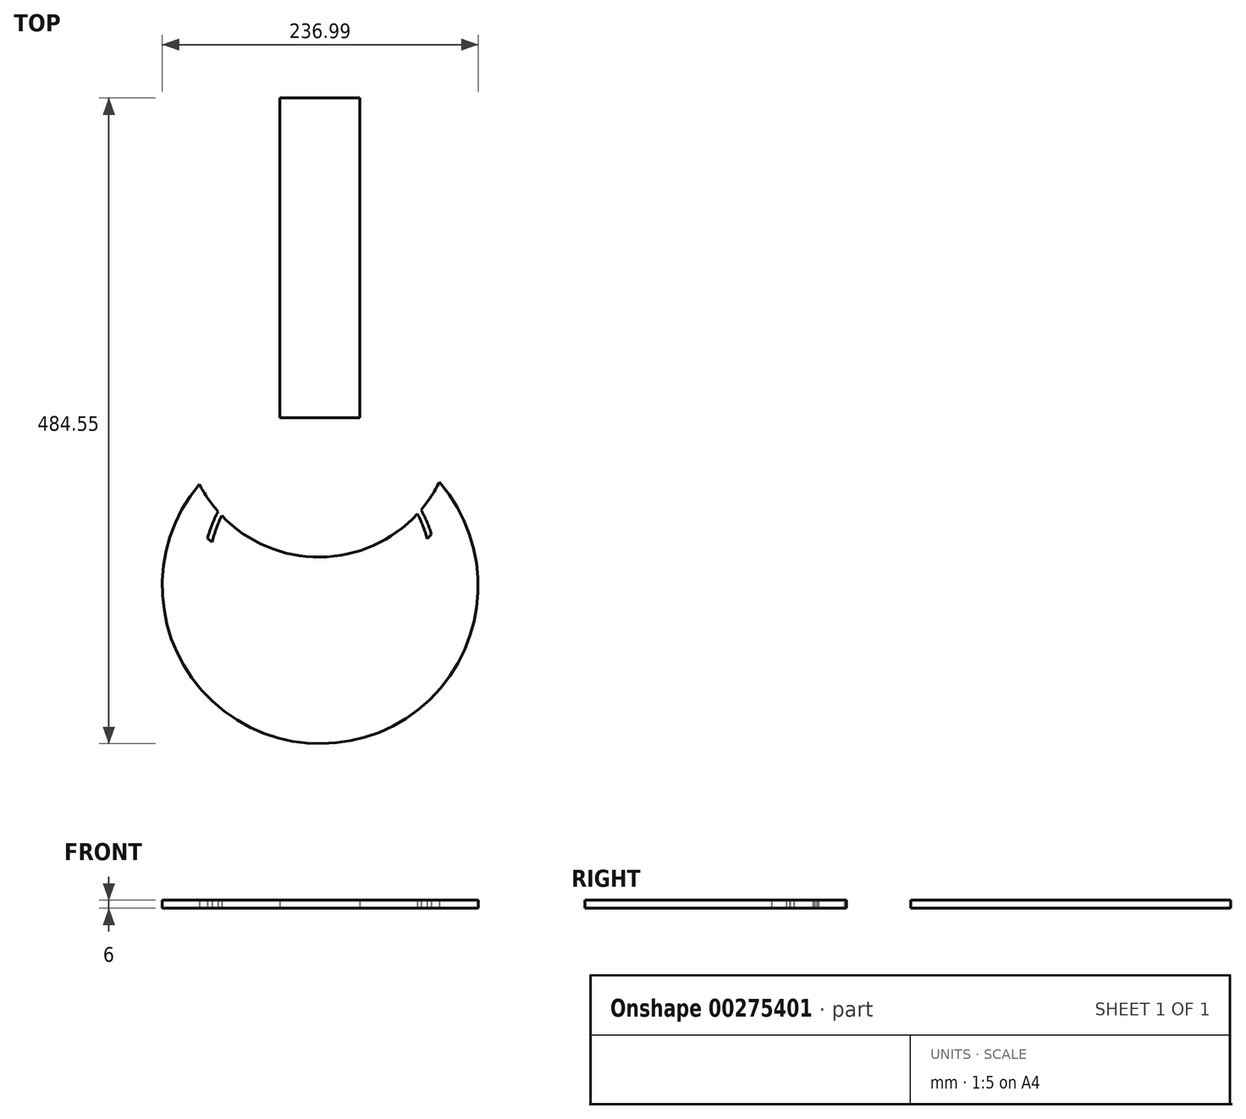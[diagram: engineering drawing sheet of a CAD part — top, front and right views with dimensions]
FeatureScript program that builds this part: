
annotation { "Feature Type Name" : "Feature", "Feature Type Description" : "" }
export const myFeature = defineFeature(function(context is Context, id is Id, definition is map)
    precondition{}
    {
        {
            var Q0;
            Q0=qCreatedBy(makeId("Top.planeOp"),FACE);
            var sketch = newSketch(context, id + "F0", { "sketchPlane" : qUnion([Q0])});
            skLineSegment(sketch, "E0.bottom", {"start": v(-25.11, 155.22) * mm, "end": v(34.89, 155.22) * mm});
            skLineSegment(sketch, "E1", {"start": v(-25.11, -64.78) * mm, "end": v(34.89, -64.78) * mm});
            skPoint(sketch, "E2.start.orphan", {"position": v(-125, -132.75) * mm});
            skLineSegment(sketch, "E3", {"start": v(0, 0) * mm, "end": v(4.89, -189.33) * mm, "construction": true});
            skPoint(sketch, "E3.endSnap0", {"position": v(4.89, -64.78) * mm});
            skLineSegment(sketch, "E4", {"start": v(4.89, -189.33) * mm, "end": v(5.87, -312.36) * mm});
            skPoint(sketch, "E4.endSnap0", {"position": v(5.87, -212.77) * mm});
            skArc(sketch, "E5", {"start": v(-85.55, -134.55) * mm, "mid": v(6.15, -329.32) * mm, "end": v(94.46, -133) * mm});
            skArc(sketch, "E6", {"start": v(-85.55, -134.55) * mm, "mid": v(4.94, -189.33) * mm, "end": v(94.46, -133) * mm});
            skPoint(sketch, "E7.startSnap0", {"position": v(4.94, -189.33) * mm});
            skLineSegment(sketch, "E8.bottom", {"start": v(-25.11, -64.78) * mm, "end": v(-25.11, -64.78) * mm});
            skLineSegment(sketch, "E9.bottom", {"start": v(34.89, -64.78) * mm, "end": v(34.89, -64.78) * mm});
            skLineSegment(sketch, "E10", {"start": v(34.89, -64.78) * mm, "end": v(34.14, -184.74) * mm});
            skLineSegment(sketch, "E11", {"start": v(-25.11, -64.78) * mm, "end": v(-25.86, -184.78) * mm});
            skLineSegment(sketch, "E12", {"start": v(34.89, 155.22) * mm, "end": v(34.89, -64.78) * mm});
            skLineSegment(sketch, "E13", {"start": v(-25.11, -64.78) * mm, "end": v(-25.11, 155.22) * mm});
            skLineSegment(sketch, "E14", {"start": v(-25.11, -64.78) * mm, "end": v(-25.24, -84.78) * mm});
            skLineSegment(sketch, "E15", {"start": v(-25.24, -84.78) * mm, "end": v(34.76, -84.78) * mm});
            skLineSegment(sketch, "E16", {"start": v(34.76, -84.78) * mm, "end": v(34.89, -64.78) * mm});
            skArc(sketch, "E17", {"start": v(-71.48, -155.21) * mm, "mid": v(5.76, -284.64) * mm, "end": v(80.75, -153.9) * mm});
            skArc(sketch, "E18", {"start": v(-68.72, -158.21) * mm, "mid": v(5.77, -278.56) * mm, "end": v(78.1, -156.9) * mm});
            skLineSegment(sketch, "E19", {"start": v(-79.46, -175.21) * mm, "end": v(-75.86, -178.21) * mm});
            skLineSegment(sketch, "E20", {"start": v(85.29, -175.56) * mm, "end": v(88.65, -172.27) * mm});
            skSolve(sketch);
        }
        {
            var Q0;
            Q0=makeQuery(id+"F0.imprint","IMPRINT",FACE,{"disambiguationData":[TD([[makeQuery(id+"F0.imprint","IMPRINT",EDGE,{"derivedFrom":sQuery(id+"F0.wireOp",EDGE,"E0.bottom")}),-1.0]])]});
            var Q1;
            {var subQ1=sQuery(id+"F0.wireOp",EDGE,"E5");Q1=makeQuery(id+"F0.imprint","IMPRINT",FACE,{"disambiguationData":[TD([[makeQuery(id+"F0.imprint","IMPRINT",EDGE,{"derivedFrom":subQ1}),1.0]])]});}
            var Q2;
            {var subQ0=sQuery(id+"F0.wireOp",EDGE,"E6");var subQ1=sQuery(id+"F0.wireOp",EDGE,"E4");var subQ2=makeQuery(id+"F0.imprint","INTERSECT",VERTEX,{"derivedFrom":[subQ1,subQ0]});Q2=makeQuery(id+"F0.imprint","IMPRINT",FACE,{"disambiguationData":[TD([[makeQuery(id+"F0.imprint","IMPRINT",EDGE,{"disambiguationData":[TD([[subQ2,-1.0]])],"derivedFrom":subQ1}),-1.0]])]});}
            var Q3;
            {var subQ0=sQuery(id+"F0.wireOp",EDGE,"E6");var subQ1=sQuery(id+"F0.wireOp",EDGE,"E4");var subQ2=makeQuery(id+"F0.imprint","INTERSECT",VERTEX,{"derivedFrom":[subQ1,subQ0]});Q3=makeQuery(id+"F0.imprint","IMPRINT",FACE,{"disambiguationData":[TD([[makeQuery(id+"F0.imprint","IMPRINT",EDGE,{"disambiguationData":[TD([[subQ2,-1.0]])],"derivedFrom":subQ1}),1.0]])]});}
            var Q4;
            {var subQ0=sQuery(id+"F0.wireOp",EDGE,"E17");var subQ1=sQuery(id+"F0.wireOp",EDGE,"E4");var subQ2=makeQuery(id+"F0.imprint","INTERSECT",VERTEX,{"derivedFrom":[subQ1,subQ0]});Q4=makeQuery(id+"F0.imprint","IMPRINT",FACE,{"disambiguationData":[TD([[makeQuery(id+"F0.imprint","IMPRINT",EDGE,{"disambiguationData":[TD([[subQ2,1.0]])],"derivedFrom":subQ1}),-1.0]])]});}
            var Q5;
            {var subQ0=sQuery(id+"F0.wireOp",EDGE,"E17");var subQ1=sQuery(id+"F0.wireOp",EDGE,"E4");var subQ2=makeQuery(id+"F0.imprint","INTERSECT",VERTEX,{"derivedFrom":[subQ1,subQ0]});Q5=makeQuery(id+"F0.imprint","IMPRINT",FACE,{"disambiguationData":[TD([[makeQuery(id+"F0.imprint","IMPRINT",EDGE,{"disambiguationData":[TD([[subQ2,1.0]])],"derivedFrom":subQ1}),1.0]])]});}
            var Q6;
            {var subQ3=sQuery(id+"F0.wireOp",EDGE,"E10");Q6=makeQuery(id+"F0.imprint","IMPRINT",FACE,{"disambiguationData":[TD([[makeQuery(id+"F0.imprint","IMPRINT",EDGE,{"derivedFrom":subQ3}),-1.0]])]});}
            var Q7;
            Q7=makeQuery(id+"F0.imprint","IMPRINT",FACE,{"disambiguationData":[TD([[makeQuery(id+"F0.imprint","IMPRINT",EDGE,{"derivedFrom":sQuery(id+"F0.wireOp",EDGE,"E1")}),-1.0]])]});
            extrude(context, id + "F1", {"entities" : qUnion([Q0, Q1, Q2, Q3, Q4, Q5, Q6, Q7]), "depth" : 6 * mm});
        }
        {
            var Q0;
            Q0=sQuery(id+"F0.wireOp",EDGE,"E18");
            var Q1;
            Q1=sQuery(id+"F0.wireOp",EDGE,"E17");
            extrude(context, id + "F2", {"bodyType" : ToolBodyType.SURFACE, "surfaceEntities" : qUnion([Q0, Q1]), "depth" : 10 * mm});
        }
    });
